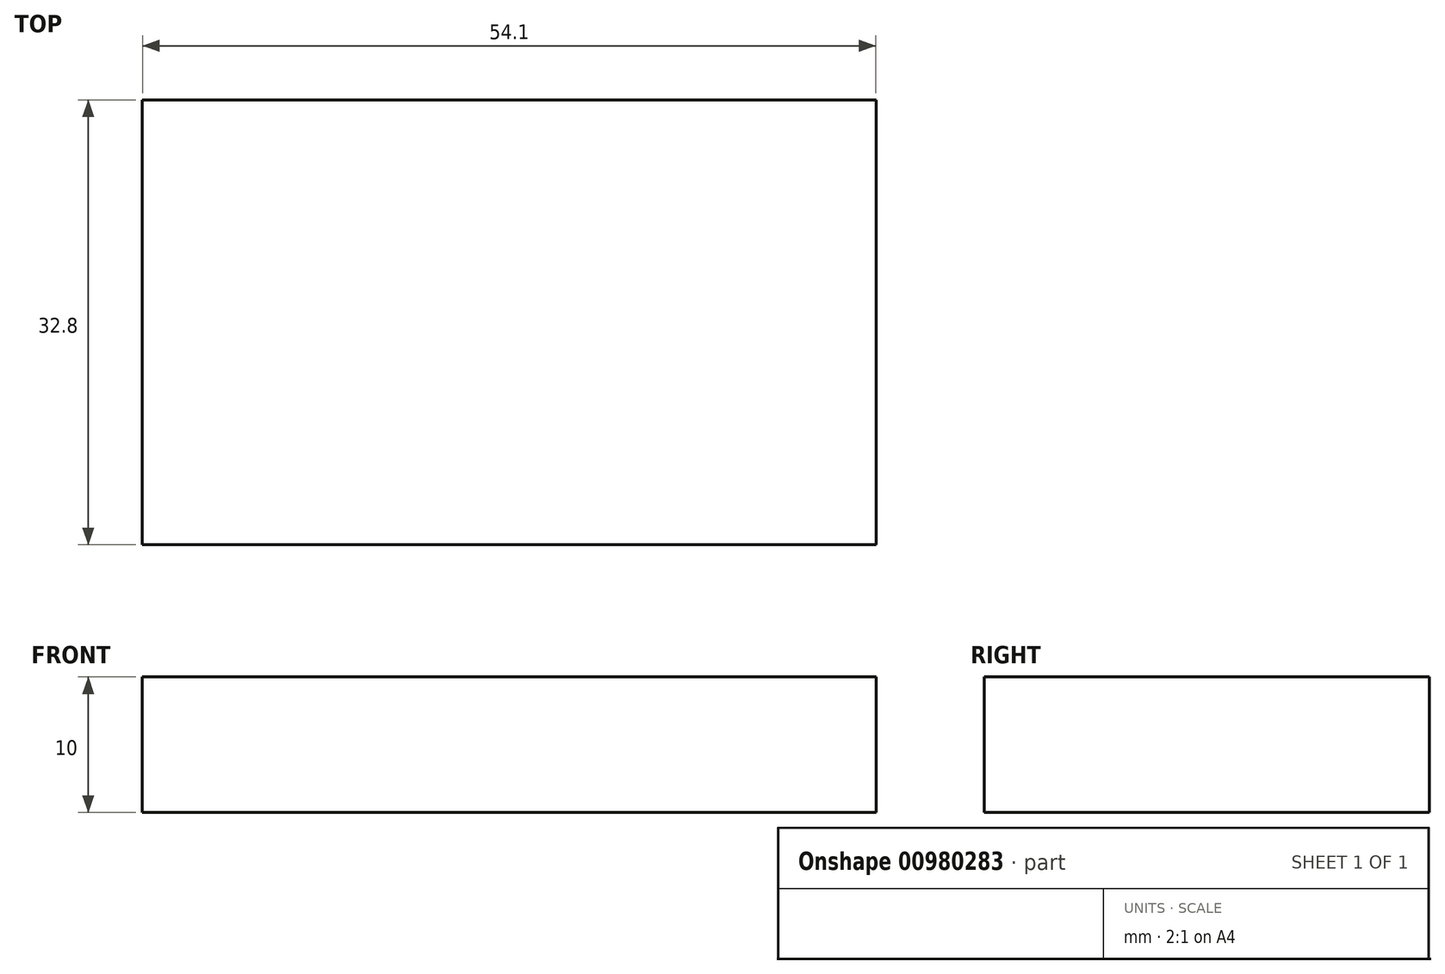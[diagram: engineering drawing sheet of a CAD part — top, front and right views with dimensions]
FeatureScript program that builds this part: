
annotation { "Feature Type Name" : "Feature", "Feature Type Description" : "" }
export const myFeature = defineFeature(function(context is Context, id is Id, definition is map)
    precondition{}
    {
        {
            var Q0;
            Q0=qCreatedBy(makeId("Top.planeOp"),FACE);
            var sketch = newSketch(context, id + "F0", { "sketchPlane" : qUnion([Q0])});
            skLineSegment(sketch, "E0.bottom", {"start": v(27.06, 16.4) * mm, "end": v(-27.05, 16.4) * mm});
            skLineSegment(sketch, "E0.top", {"start": v(27.06, -16.4) * mm, "end": v(-27.05, -16.4) * mm});
            skLineSegment(sketch, "E0.left", {"start": v(27.06, 16.4) * mm, "end": v(27.06, -16.4) * mm});
            skLineSegment(sketch, "E0.right", {"start": v(-27.05, 16.4) * mm, "end": v(-27.05, -16.4) * mm});
            skPoint(sketch, "E0.middle", {"position": v(0, 0) * mm});
            skSolve(sketch);
        }
        {
            var Q0;
            Q0 = qSketchRegion(id + "F0", true);
            extrude(context, id + "F1", {"entities" : qUnion([Q0]), "depth" : 10 * mm, "offsetDistance" : 25 * mm});
        }
    });
